# Revit family: Grid_Drain-American_Standard-Heritage-7716020.002
name_source: partatom
category: Plumbing Fixtures
units: mm (PartAtom-declared; Revit-internal decimal feet)

## family parameters
Always vertical = No
Cut with Voids When Loaded = No
OmniClass Number = 23.70.50.21.24
OmniClass Title = Waste Water Drains
Part Type = Normal
Room Calculation Point = No
Round Connector Dimension = Use Diameter
Shared = Yes
Work Plane-Based = Yes

## types (1)
- 7716020.002
    Assembly Code = D2030300
    CW Connection = No
    CWFU = 3
    Cost = $0
    Default Elevation = 34"
    Description = Grid Strainer Drain for Sinks
    Diameter = 2 31/32"
    Drain Screw Length = 1 1/4"
    Drain Screw Length Constraint = 1 1/4"
    Finish = Brass-American Standard-002-Chrome
    HW Connection = No
    HWFU = 3
    Height = 6 13/16"
    IAPMO Compliance = ASME A112.18.2 and CSA B 125.2
    Installation Type = Surface Mounted
    Manufacturer = American Standard
    Material = Brass-American Standard-002-Chrome
    Model = 7716020.002
    Product Documentation Link = https://americanstandard.box.com
    Product Page URL = https://americanstandard-us.com
    Revised Date = 08/04/2022
    URL = https://www.americanstandard-us.com
    Vent Connection = No
    WFU = 4
    Waste Connection = Yes
    Waste Connection Diameter = 1 1/2"

## geometry (parser evidence)
native form markers: Sweep x2
no freeform markers — native parametric forms only
